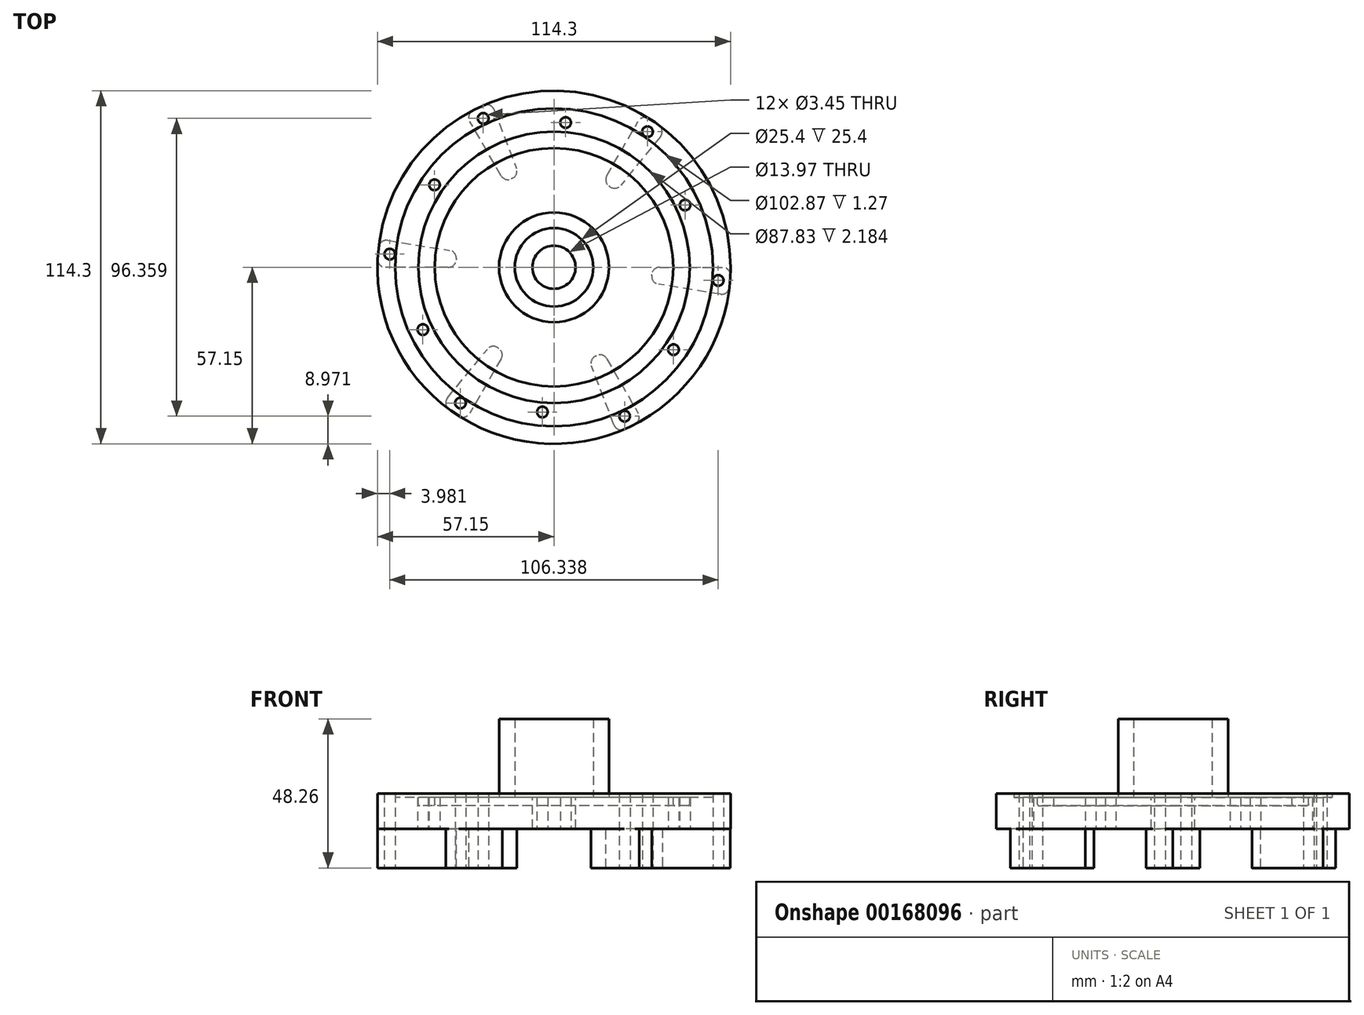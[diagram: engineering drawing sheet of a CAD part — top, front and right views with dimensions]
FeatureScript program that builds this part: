
annotation { "Feature Type Name" : "Feature", "Feature Type Description" : "" }
export const myFeature = defineFeature(function(context is Context, id is Id, definition is map)
    precondition{}
    {
        {
            var Q0;
            Q0=qCreatedBy(makeId("Top.planeOp"),FACE);
            var sketch = newSketch(context, id + "F0", { "sketchPlane" : qUnion([Q0])});
            skCircle(sketch, "E0", {"center": v(0, 0) * mm, "radius": 57.15 * mm});
            skSolve(sketch);
        }
        {
            var Q0;
            Q0=makeQuery(id+"F0.imprint","IMPRINT",FACE,{"disambiguationData":[TD([[makeQuery(id+"F0.imprint","IMPRINT",EDGE,{"derivedFrom":sQuery(id+"F0.wireOp",EDGE,"E0")}),1.0]])]});
            extrude(context, id + "F1", {"entities" : qUnion([Q0]), "depth" : 10.16 * mm});
        }
        {
            var Q0;
            Q0=makeQuery(id+"F1.opExtrude","CAP_FACE",FACE,{"disambiguationData":[OSD([sQuery(id+"F0.wireOp",EDGE,"E0")])],"isStart":false});
            var sketch = newSketch(context, id + "F2", { "sketchPlane" : qUnion([Q0])});
            skCircle(sketch, "E1", {"center": v(0, 0) * mm, "radius": 17.78 * mm});
            skCircle(sketch, "E2", {"center": v(0, 0) * mm, "radius": 12.7 * mm});
            skSolve(sketch);
        }
        {
            var Q0;
            Q0=qSketchRegion(id+"F2",true);
            extrude(context, id + "F3", {"entities" : qUnion([Q0]), "operationType" : NewBodyOperationType.ADD, "depth" : 25.4 * mm});
        }
        {
            var Q0;
            Q0=makeQuery(id+"F3.boolean.opBoolean","SPLIT",FACE,{"disambiguationData":[TD([makeQuery(id+"F3.opExtrude","SWEPT_FACE",FACE,{"disambiguationData":[OSD([sQuery(id+"F2.wireOp",EDGE,"E2")])]})])],"derivedFrom":makeQuery(id+"F1.opExtrude","CAP_FACE",FACE,{"disambiguationData":[OSD([sQuery(id+"F0.wireOp",EDGE,"E0")])],"isStart":false})});
            var sketch = newSketch(context, id + "F4", { "sketchPlane" : qUnion([Q0])});
            skCircle(sketch, "E3", {"center": v(0, 0) * mm, "radius": 6.99 * mm});
            skSolve(sketch);
        }
        {
            var Q0;
            Q0=qSketchRegion(id+"F4",true);
            extrude(context, id + "F5", {"entities" : qUnion([Q0]), "operationType" : NewBodyOperationType.REMOVE, "endBound" : BoundingType.THROUGH_ALL, "oppositeDirection" : true, "depth" : 25.4 * mm});
        }
        {
            var Q0;
            Q0=makeQuery(id+"F1.opExtrude","CAP_FACE",FACE,{"disambiguationData":[OSD([sQuery(id+"F0.wireOp",EDGE,"E0")])],"isStart":true});
            var sketch = newSketch(context, id + "F6", { "sketchPlane" : qUnion([Q0])});
            skArc(sketch, "E4", {"start": v(-57.15, 0) * mm, "mid": v(-56.97, -4.57) * mm, "end": v(-56.42, -9.11) * mm});
            skArc(sketch, "E5", {"start": v(-31.75, 0) * mm, "mid": v(-31.65, -2.54) * mm, "end": v(-31.34, -5.06) * mm});
            skLineSegment(sketch, "E6", {"start": v(0, 0) * mm, "end": v(-31.34, -5.06) * mm, "construction": true});
            skLineSegment(sketch, "E7", {"start": v(-56.42, -9.11) * mm, "end": v(-31.34, -5.06) * mm});
            skLineSegment(sketch, "E8", {"start": v(-31.75, 0) * mm, "end": v(-57.15, 0) * mm});
            skSolve(sketch);
        }
        {
            var Q0;
            Q0=qSketchRegion(id+"F6",true);
            extrude(context, id + "F7", {"entities" : qUnion([Q0]), "operationType" : NewBodyOperationType.ADD, "depth" : 12.7 * mm});
        }
        {
            var Q0;
            Q0=makeQuery(id+"F7.opExtrude","SWEPT_EDGE",EDGE,{"disambiguationData":[OSD([sQuery(id+"F0.wireOp",EDGE,"E0"),sQuery(id+"F6.wireOp",EDGE,"E4"),sQuery(id+"F6.wireOp",EDGE,"E7")])]});
            var Q1;
            Q1=makeQuery(id+"F7.opExtrude","SWEPT_EDGE",EDGE,{"disambiguationData":[OSD([sQuery(id+"F6.wireOp",EDGE,"E5"),sQuery(id+"F6.wireOp",EDGE,"E7")])]});
            var Q2;
            Q2=makeQuery(id+"F7.opExtrude","SWEPT_EDGE",EDGE,{"disambiguationData":[OSD([sQuery(id+"F0.wireOp",EDGE,"E0"),sQuery(id+"F6.wireOp",EDGE,"E4"),sQuery(id+"F6.wireOp",EDGE,"E8")])]});
            var Q3;
            Q3=makeQuery(id+"F7.opExtrude","SWEPT_EDGE",EDGE,{"disambiguationData":[OSD([sQuery(id+"F6.wireOp",EDGE,"E5"),sQuery(id+"F6.wireOp",EDGE,"E8")])]});
            fillet(context, id + "F8", {"entities" : qUnion([Q0, Q1, Q2, Q3]), "radius" : 2.54 * mm, "tangentPropagation" : true, "allowEdgeOverflow" : false});
        }
        {
            var Q0;
            Q0=makeQuery(id+"F7.opExtrude","CAP_FACE",FACE,{"disambiguationData":[OSD([sQuery(id+"F6.wireOp",EDGE,"E4"),sQuery(id+"F6.wireOp",EDGE,"E5"),sQuery(id+"F6.wireOp",EDGE,"E7"),sQuery(id+"F6.wireOp",EDGE,"E8")])],"isStart":false});
            var sketch = newSketch(context, id + "F9", { "sketchPlane" : qUnion([Q0])});
            skLineSegment(sketch, "E9", {"start": v(-54.55, 0) * mm, "end": v(-53.85, -8.7) * mm, "construction": true});
            skPoint(sketch, "E10", {"position": v(-54.2, -4.35) * mm});
            skLineSegment(sketch, "E11", {"start": v(0, 0) * mm, "end": v(-54.2, -4.35) * mm, "construction": true});
            skLineSegment(sketch, "E12", {"start": v(-54.2, -4.35) * mm, "end": v(-80.75, -6.48) * mm, "construction": true});
            skPoint(sketch, "E13.3.0", {"position": v(-53.17, -4.27) * mm});
            skPoint(sketch, "E13.center", {"position": v(0, 0) * mm});
            skPoint(sketch, "E14.1.0", {"position": v(-22.89, -48.18) * mm});
            skPoint(sketch, "E14.2.0", {"position": v(30.28, -43.91) * mm});
            skPoint(sketch, "E15.0.3.0", {"position": v(53.17, 4.27) * mm});
            skPoint(sketch, "E15.0.4.0", {"position": v(22.89, 48.18) * mm});
            skPoint(sketch, "E15.0.5.0", {"position": v(-30.28, 43.91) * mm});
            skSolve(sketch);
        }
        {
            var Q0;
            Q0=makeQuery(id+"F1.opExtrude","SWEPT_BODY",BODY,{"disambiguationData":[OSD([sQuery(id+"F0.wireOp",EDGE,"E0")])]});
            var Q1;
            Q1=makeQuery(id+"F5.boolean.opBoolean","COPY",FACE,{"derivedFrom":makeQuery(id+"F5.opExtrude","SWEPT_FACE",FACE,{"disambiguationData":[OSD([sQuery(id+"F4.wireOp",EDGE,"E3")])]})});
            circularPattern(context, id + "F10", {"operationType" : NewBodyOperationType.ADD, "entities" : qUnion([Q0]), "axis" : qUnion([Q1]), "angle" : 360 * degree, "instanceCount" : 6, "equalSpace" : true});
        }
        {
            var Q0;
            {var subQ0=sQuery(id+"F0.wireOp",EDGE,"E0");Q0=makeQuery(id+"F3.boolean.opBoolean","SPLIT",FACE,{"disambiguationData":[TD([makeQuery(id+"F1.opExtrude","SWEPT_FACE",FACE,{"disambiguationData":[OSD([subQ0])]})])],"derivedFrom":makeQuery(id+"F1.opExtrude","CAP_FACE",FACE,{"disambiguationData":[OSD([subQ0])],"isStart":false})});}
            var sketch = newSketch(context, id + "F11", { "sketchPlane" : qUnion([Q0])});
            skCircle(sketch, "E16.0", {"center": v(0, 0) * mm, "radius": 57.15 * mm});
            skCircle(sketch, "E17", {"center": v(0, 0) * mm, "radius": 51.44 * mm});
            skSolve(sketch);
        }
        {
            var Q0;
            Q0=qSketchRegion(id+"F11",true);
            extrude(context, id + "F12", {"entities" : qUnion([Q0]), "operationType" : NewBodyOperationType.ADD, "depth" : 1.27 * mm});
        }
        {
            var Q0;
            Q0=sQuery(id+"F9.wireOp",VERTEX,"E13.3.0");
            var Q1;
            Q1=sQuery(id+"F9.wireOp",VERTEX,"E14.1.0");
            var Q2;
            Q2=sQuery(id+"F9.wireOp",VERTEX,"E14.2.0");
            var Q3;
            Q3=sQuery(id+"F9.wireOp",VERTEX,"E15.0.3.0");
            var Q4;
            Q4=sQuery(id+"F9.wireOp",VERTEX,"E15.0.4.0");
            var Q5;
            Q5=sQuery(id+"F9.wireOp",VERTEX,"E15.0.5.0");
            var Q6;
            Q6=makeQuery(id+"F1.opExtrude","SWEPT_BODY",BODY,{"disambiguationData":[OSD([sQuery(id+"F0.wireOp",EDGE,"E0")])]});
            hole(context, id + "F13", {"style" : HoleStyle.SIMPLE, "endStyle" : HoleEndStyle.THROUGH, "standardTappedOrClearance" : lookupTablePath({ "standard" : "ANSI", "engagement" : "75%", "pitch" : "32 tpi", "size" : "#8", "type" : "Tapped" }), "standardBlindInLast" : lookupTablePath({ "standard" : "ANSI", "engagement" : "75%", "pitch" : "32 tpi", "size" : "#8", "type" : "Tapped" }), "holeDiameter" : 3.45 * mm, "locations" : qUnion([Q0, Q1, Q2, Q3, Q4, Q5]), "scope" : qUnion([Q6]), "isTappedThrough" : true, "majorDiameter" : 4.17 * mm, "showTappedDepth" : true});
        }
        {
            var Q0;
            {var subQ0=sQuery(id+"F0.wireOp",EDGE,"E0");Q0=makeQuery(id+"F3.boolean.opBoolean","SPLIT",FACE,{"disambiguationData":[TD([makeQuery(id+"F1.opExtrude","SWEPT_FACE",FACE,{"disambiguationData":[OSD([subQ0])]})])],"derivedFrom":makeQuery(id+"F1.opExtrude","CAP_FACE",FACE,{"disambiguationData":[OSD([subQ0])],"isStart":false})});}
            var sketch = newSketch(context, id + "F14", { "sketchPlane" : qUnion([Q0])});
            skCircle(sketch, "E18", {"center": v(0, 0) * mm, "radius": 41.25 * mm, "construction": true});
            skCircle(sketch, "E19", {"center": v(0, 0) * mm, "radius": 38.58 * mm});
            skCircle(sketch, "E20", {"center": v(0, 0) * mm, "radius": 43.92 * mm});
            skSolve(sketch);
        }
        {
            var Q0;
            Q0=qSketchRegion(id+"F14",true);
            extrude(context, id + "F15", {"entities" : qUnion([Q0]), "operationType" : NewBodyOperationType.REMOVE, "oppositeDirection" : true, "depth" : 2.7 * mm});
        }
        {
            var Q0;
            Q0=makeQuery(id+"F15.boolean.opBoolean","COPY",EDGE,{"derivedFrom":makeQuery(id+"F15.opExtrude","CAP_EDGE",EDGE,{"disambiguationData":[OSD([sQuery(id+"F14.wireOp",EDGE,"E20")])],"isStart":false})});
            var Q1;
            Q1=makeQuery(id+"F15.boolean.opBoolean","COPY",EDGE,{"derivedFrom":makeQuery(id+"F15.opExtrude","CAP_EDGE",EDGE,{"disambiguationData":[OSD([sQuery(id+"F14.wireOp",EDGE,"E19")])],"isStart":false})});
            fillet(context, id + "F16", {"entities" : qUnion([Q0, Q1]), "radius" : 0.5 * mm, "tangentPropagation" : true, "allowEdgeOverflow" : false});
        }
        {
            var Q0;
            Q0=makeQuery(id+"F1.opExtrude","CAP_FACE",FACE,{"disambiguationData":[OSD([sQuery(id+"F0.wireOp",EDGE,"E0")])],"isStart":true});
            var sketch = newSketch(context, id + "F17", { "sketchPlane" : qUnion([Q0])});
            skLineSegment(sketch, "E21", {"start": v(-53.85, -8.7) * mm, "end": v(-27.28, -47.24) * mm, "construction": true});
            skLineSegment(sketch, "E22", {"start": v(0, 0) * mm, "end": v(-40.56, -27.97) * mm, "construction": true});
            skPoint(sketch, "E23", {"position": v(-38.68, -26.68) * mm});
            skPoint(sketch, "E24.1.0", {"position": v(3.76, -46.84) * mm});
            skPoint(sketch, "E24.2.0", {"position": v(42.44, -20.16) * mm});
            skPoint(sketch, "E24.3.0", {"position": v(38.68, 26.68) * mm});
            skPoint(sketch, "E24.4.0", {"position": v(-3.76, 46.84) * mm});
            skPoint(sketch, "E24.5.0", {"position": v(-42.44, 20.16) * mm});
            skPoint(sketch, "E24.center", {"position": v(0, 0) * mm});
            skSolve(sketch);
        }
        {
            var Q0;
            Q0=sQuery(id+"F17.wireOp",VERTEX,"E23");
            var Q1;
            Q1=sQuery(id+"F17.wireOp",VERTEX,"E24.1.0");
            var Q2;
            Q2=sQuery(id+"F17.wireOp",VERTEX,"E24.2.0");
            var Q3;
            Q3=sQuery(id+"F17.wireOp",VERTEX,"E24.3.0");
            var Q4;
            Q4=sQuery(id+"F17.wireOp",VERTEX,"E24.4.0");
            var Q5;
            Q5=sQuery(id+"F17.wireOp",VERTEX,"E24.5.0");
            var Q6;
            Q6=makeQuery(id+"F1.opExtrude","SWEPT_BODY",BODY,{"disambiguationData":[OSD([sQuery(id+"F0.wireOp",EDGE,"E0")])]});
            hole(context, id + "F18", {"style" : HoleStyle.SIMPLE, "endStyle" : HoleEndStyle.THROUGH, "standardTappedOrClearance" : lookupTablePath({ "standard" : "ANSI", "engagement" : "75%", "pitch" : "32 tpi", "size" : "#8", "type" : "Tapped" }), "standardBlindInLast" : lookupTablePath({ "standard" : "ANSI", "engagement" : "75%", "pitch" : "32 tpi", "size" : "#8", "type" : "Tapped" }), "holeDiameter" : 3.45 * mm, "locations" : qUnion([Q0, Q1, Q2, Q3, Q4, Q5]), "scope" : qUnion([Q6]), "isTappedThrough" : true, "majorDiameter" : 4.17 * mm, "showTappedDepth" : true});
        }
    });
